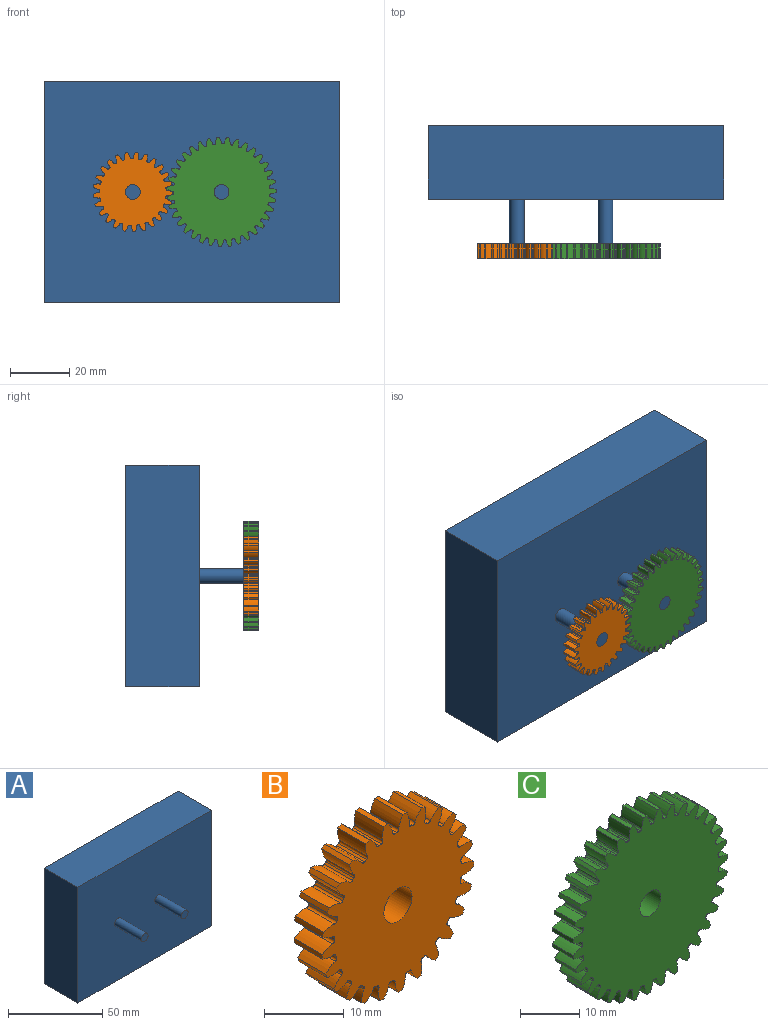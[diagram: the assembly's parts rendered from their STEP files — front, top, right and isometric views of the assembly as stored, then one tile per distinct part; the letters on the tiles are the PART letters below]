
ASSEMBLY  parts=3 mates=2
PART A: 10 faces, bbox 100x45x75 mm
  f0: plane 75x25mm, normal (1,0,0), area 1875mm2, adj f1,f3,f4,f5
  f1: plane 100x25mm, normal (0,0,1), area 2500mm2, adj f0,f2,f4,f5
  f2: plane 75x25mm, normal (-1,0,0), area 1875mm2, adj f1,f3,f4,f5
  f3: plane 100x25mm, normal (0,0,-1), area 2500mm2, adj f0,f2,f4,f5
  f4: plane 100x75mm, normal (0,1,0), area 7500mm2, adj f0,f1,f2,f3
  f5: plane 100x75mm, normal (0,-1,0), area 7460.7mm2, adj f0,f1,f2,f3,f6,f8
  f6: cylinder r=2.5mm len=20mm, axis (0,1,0), area 314.2mm2, adj f5,f7
  f7: plane 5x5mm, normal (0,-1,0), area 19.6mm2, adj f6
  f8: cylinder r=2.5mm len=20mm, axis (0,1,0), area 314.2mm2, adj f5,f9
  f9: plane 5x5mm, normal (0,-1,0), area 19.6mm2, adj f8
PART B: 153 faces, bbox 27x5x27 mm
  f0: extruded ~5x1.91mm, area 10.1mm2, adj f100,f101,f102,f103
  f1: cylinder r=11.25mm len=5mm, axis (0,1,0), area 1.9mm2, adj f101,f102,f103,f104
  f2: extruded ~5x1.76mm, area 10.1mm2, adj f3,f101,f102,f104
  f3: cylinder r=13.5mm len=5mm, axis (0,1,0), area 3.6mm2, adj f2,f4,f101,f102
  f4: extruded ~5x2mm, area 10.1mm2, adj f3,f101,f102,f105
  f5: cylinder r=11.25mm len=5mm, axis (0,1,0), area 1.9mm2, adj f101,f102,f105,f106
  f6: extruded ~5x1.47mm, area 10.1mm2, adj f7,f101,f102,f106
  f7: cylinder r=13.5mm len=5mm, axis (0,1,0), area 3.6mm2, adj f6,f8,f101,f102
  f8: extruded ~5x1.96mm, area 10.1mm2, adj f7,f101,f102,f107
  f9: cylinder r=11.25mm len=5mm, axis (0,1,0), area 1.9mm2, adj f101,f102,f107,f108
  f10: extruded ~5x1.68mm, area 10.1mm2, adj f11,f101,f102,f108
  f11: cylinder r=13.5mm len=5mm, axis (0,1,0), area 3.6mm2, adj f10,f12,f101,f102
  f12: extruded ~5x1.8mm, area 10.1mm2, adj f11,f101,f102,f109
  f13: cylinder r=11.25mm len=5mm, axis (0,1,0), area 1.9mm2, adj f101,f102,f109,f110
  f14: extruded ~5x1.9mm, area 10.1mm2, adj f15,f101,f102,f110
  f15: cylinder r=13.5mm len=5mm, axis (0,1,0), area 3.6mm2, adj f14,f16,f101,f102
  f16: extruded ~5x1.53mm, area 10.1mm2, adj f15,f101,f102,f111
  f17: cylinder r=11.25mm len=5mm, axis (0,1,0), area 1.9mm2, adj f101,f102,f111,f112
  f18: extruded ~5x2mm, area 10.1mm2, adj f19,f101,f102,f112
  f19: cylinder r=13.5mm len=5mm, axis (0,1,0), area 3.6mm2, adj f18,f20,f101,f102
  f20: extruded ~5x1.63mm, area 10.1mm2, adj f19,f101,f102,f113
  f21: cylinder r=11.25mm len=5mm, axis (0,1,0), area 1.9mm2, adj f101,f102,f113,f114
  f22: extruded ~5x1.97mm, area 10.1mm2, adj f23,f101,f102,f114
  f23: cylinder r=13.5mm len=5mm, axis (0,1,0), area 3.6mm2, adj f22,f24,f101,f102
  f24: extruded ~5x1.87mm, area 10.1mm2, adj f23,f101,f102,f115
  f25: cylinder r=11.25mm len=5mm, axis (0,1,0), area 1.9mm2, adj f101,f102,f115,f116
  f26: extruded ~5x1.82mm, area 10.1mm2, adj f27,f101,f102,f116
  f27: cylinder r=13.5mm len=5mm, axis (0,1,0), area 3.6mm2, adj f26,f28,f101,f102
  f28: extruded ~5x1.99mm, area 10.1mm2, adj f27,f101,f102,f117
  f29: cylinder r=11.25mm len=5mm, axis (0,1,0), area 1.9mm2, adj f101,f102,f117,f118
  f30: extruded ~5x1.55mm, area 10.1mm2, adj f31,f101,f102,f118
  f31: cylinder r=13.5mm len=5mm, axis (0,1,0), area 3.6mm2, adj f30,f32,f101,f102
  f32: extruded ~5x1.98mm, area 10.1mm2, adj f31,f101,f102,f119
  f33: cylinder r=11.25mm len=5mm, axis (0,1,0), area 1.9mm2, adj f101,f102,f119,f120
  f34: extruded ~5x1.61mm, area 10.1mm2, adj f35,f101,f102,f120
  f35: cylinder r=13.5mm len=5mm, axis (0,1,0), area 3.6mm2, adj f34,f36,f101,f102
  f36: extruded ~5x1.85mm, area 10.1mm2, adj f35,f101,f102,f121
  f37: cylinder r=11.25mm len=5mm, axis (0,1,0), area 1.9mm2, adj f101,f102,f121,f122
  f38: extruded ~5x1.86mm, area 10.1mm2, adj f39,f101,f102,f122
  f39: cylinder r=13.5mm len=5mm, axis (0,1,0), area 3.6mm2, adj f38,f40,f101,f102
  f40: extruded ~5x1.61mm, area 10.1mm2, adj f39,f101,f102,f123
  f41: cylinder r=11.25mm len=5mm, axis (0,1,0), area 1.9mm2, adj f101,f102,f123,f124
  f42: extruded ~5x1.98mm, area 10.1mm2, adj f43,f101,f102,f124
  f43: cylinder r=13.5mm len=5mm, axis (0,1,0), area 3.6mm2, adj f42,f44,f101,f102
  f44: extruded ~5x1.56mm, area 10.1mm2, adj f43,f101,f102,f125
  f45: cylinder r=11.25mm len=5mm, axis (0,1,0), area 1.9mm2, adj f101,f102,f125,f126
  f46: extruded ~5x1.99mm, area 10.1mm2, adj f47,f101,f102,f126
  f47: cylinder r=13.5mm len=5mm, axis (0,1,0), area 3.6mm2, adj f46,f48,f101,f102
  f48: extruded ~5x1.82mm, area 10.1mm2, adj f47,f101,f102,f127
  f49: cylinder r=11.25mm len=5mm, axis (0,1,0), area 1.9mm2, adj f101,f102,f127,f128
  f50: extruded ~5x1.87mm, area 10.1mm2, adj f51,f101,f102,f128
  f51: cylinder r=13.5mm len=5mm, axis (0,1,0), area 3.6mm2, adj f50,f52,f101,f102
  f52: extruded ~5x1.97mm, area 10.1mm2, adj f51,f101,f102,f129
  f53: cylinder r=11.25mm len=5mm, axis (0,1,0), area 1.9mm2, adj f101,f102,f129,f130
  f54: extruded ~5x1.63mm, area 10.1mm2, adj f55,f101,f102,f130
  f55: cylinder r=13.5mm len=5mm, axis (0,1,0), area 3.6mm2, adj f54,f56,f101,f102
  f56: extruded ~5x2mm, area 10.1mm2, adj f55,f101,f102,f131
  f57: cylinder r=11.25mm len=5mm, axis (0,1,0), area 1.9mm2, adj f101,f102,f131,f132
  f58: extruded ~5x1.53mm, area 10.1mm2, adj f59,f101,f102,f132
  f59: cylinder r=13.5mm len=5mm, axis (0,1,0), area 3.6mm2, adj f58,f60,f101,f102
  f60: extruded ~5x1.9mm, area 10.1mm2, adj f59,f101,f102,f133
  f61: cylinder r=11.25mm len=5mm, axis (0,1,0), area 1.9mm2, adj f101,f102,f133,f134
  f62: extruded ~5x1.81mm, area 10.1mm2, adj f63,f101,f102,f134
  f63: cylinder r=13.5mm len=5mm, axis (0,1,0), area 3.6mm2, adj f62,f64,f101,f102
  f64: extruded ~5x1.68mm, area 10.1mm2, adj f63,f101,f102,f135
  f65: cylinder r=11.25mm len=5mm, axis (0,1,0), area 1.9mm2, adj f101,f102,f135,f136
  f66: extruded ~5x1.96mm, area 10.1mm2, adj f67,f101,f102,f136
  f67: cylinder r=13.5mm len=5mm, axis (0,1,0), area 3.6mm2, adj f66,f68,f101,f102
  f68: extruded ~5x1.47mm, area 10.1mm2, adj f67,f101,f102,f137
  f69: cylinder r=11.25mm len=5mm, axis (0,1,0), area 1.9mm2, adj f101,f102,f137,f138
  f70: extruded ~5x2mm, area 10.1mm2, adj f71,f101,f102,f138
  f71: cylinder r=13.5mm len=5mm, axis (0,1,0), area 3.6mm2, adj f70,f72,f101,f102
  f72: extruded ~5x1.76mm, area 10.1mm2, adj f71,f101,f102,f139
  f73: cylinder r=11.25mm len=5mm, axis (0,1,0), area 1.9mm2, adj f101,f102,f139,f140
  f74: extruded ~5x1.91mm, area 10.1mm2, adj f75,f101,f102,f140
  f75: cylinder r=13.5mm len=5mm, axis (0,1,0), area 3.6mm2, adj f74,f76,f101,f102
  f76: extruded ~5x1.94mm, area 10.1mm2, adj f75,f101,f102,f141
  f77: cylinder r=11.25mm len=5mm, axis (0,1,0), area 1.9mm2, adj f101,f102,f141,f142
  f78: extruded ~5x1.7mm, area 10.1mm2, adj f79,f101,f102,f142
  f79: cylinder r=13.5mm len=5mm, axis (0,1,0), area 3.6mm2, adj f78,f80,f101,f102
  f80: extruded ~5x2mm, area 10.1mm2, adj f79,f101,f102,f143
  f81: cylinder r=11.25mm len=5mm, axis (0,1,0), area 1.9mm2, adj f101,f102,f143,f144
  f82: extruded ~5x1.45mm, area 10.1mm2, adj f83,f101,f102,f144
  f83: cylinder r=13.5mm len=5mm, axis (0,1,0), area 3.6mm2, adj f82,f84,f101,f102
  f84: extruded ~5x1.93mm, area 10.1mm2, adj f83,f101,f102,f145
  f85: cylinder r=11.25mm len=5mm, axis (0,1,0), area 1.9mm2, adj f101,f102,f145,f146
  f86: extruded ~5x1.75mm, area 10.1mm2, adj f87,f101,f102,f146
  f87: cylinder r=13.5mm len=5mm, axis (0,1,0), area 3.6mm2, adj f86,f88,f101,f102
  f88: extruded ~5x1.74mm, area 10.1mm2, adj f87,f101,f102,f147
  f89: cylinder r=11.25mm len=5mm, axis (0,1,0), area 1.9mm2, adj f101,f102,f147,f148
  f90: extruded ~5x1.94mm, area 10.1mm2, adj f91,f101,f102,f148
  f91: cylinder r=13.5mm len=5mm, axis (0,1,0), area 3.6mm2, adj f90,f92,f101,f102
  f92: extruded ~5x1.45mm, area 10.1mm2, adj f91,f101,f102,f149
  f93: cylinder r=11.25mm len=5mm, axis (0,1,0), area 1.9mm2, adj f101,f102,f149,f150
  f94: extruded ~5x2mm, area 10.1mm2, adj f95,f101,f102,f150
  f95: cylinder r=13.5mm len=5mm, axis (0,1,0), area 3.6mm2, adj f94,f96,f101,f102
  f96: extruded ~5x1.7mm, area 10.1mm2, adj f95,f101,f102,f151
  f97: cylinder r=11.25mm len=5mm, axis (0,1,0), area 1.9mm2, adj f101,f102,f151,f152
  f98: extruded ~5x1.94mm, area 10.1mm2, adj f100,f101,f102,f152
  f99: cylinder r=2.5mm len=5mm, axis (0,1,0), area 78.5mm2, adj f101,f102
  f100: cylinder r=13.5mm len=5mm, axis (0,1,0), area 3.6mm2, adj f0,f98,f101,f102
  f101: plane 26.98x26.97mm, normal (0,-1,0), area 463.9mm2, adj f0,f1,f2,f3,f4,f5,f6,f7
  f102: plane 26.98x26.97mm, normal (0,1,0), area 463.9mm2, adj f0,f1,f2,f3,f4,f5,f6,f7
  f103: cylinder r=0.36mm len=5mm, axis (0,1,0), area 2.8mm2, adj f0,f1,f101,f102
  f104: cylinder r=0.36mm len=5mm, axis (0,1,0), area 2.8mm2, adj f1,f2,f101,f102
  f105: cylinder r=0.36mm len=5mm, axis (0,1,0), area 2.8mm2, adj f4,f5,f101,f102
  f106: cylinder r=0.36mm len=5mm, axis (0,1,0), area 2.8mm2, adj f5,f6,f101,f102
  f107: cylinder r=0.36mm len=5mm, axis (0,1,0), area 2.8mm2, adj f8,f9,f101,f102
  f108: cylinder r=0.36mm len=5mm, axis (0,1,0), area 2.8mm2, adj f9,f10,f101,f102
  f109: cylinder r=0.36mm len=5mm, axis (0,1,0), area 2.8mm2, adj f12,f13,f101,f102
  f110: cylinder r=0.36mm len=5mm, axis (0,1,0), area 2.8mm2, adj f13,f14,f101,f102
  f111: cylinder r=0.36mm len=5mm, axis (0,1,0), area 2.8mm2, adj f16,f17,f101,f102
  f112: cylinder r=0.36mm len=5mm, axis (0,1,0), area 2.8mm2, adj f17,f18,f101,f102
  f113: cylinder r=0.36mm len=5mm, axis (0,1,0), area 2.8mm2, adj f20,f21,f101,f102
  f114: cylinder r=0.36mm len=5mm, axis (0,1,0), area 2.8mm2, adj f21,f22,f101,f102
  f115: cylinder r=0.36mm len=5mm, axis (0,1,0), area 2.8mm2, adj f24,f25,f101,f102
  f116: cylinder r=0.36mm len=5mm, axis (0,1,0), area 2.8mm2, adj f25,f26,f101,f102
  f117: cylinder r=0.36mm len=5mm, axis (0,1,0), area 2.8mm2, adj f28,f29,f101,f102
  f118: cylinder r=0.36mm len=5mm, axis (0,1,0), area 2.8mm2, adj f29,f30,f101,f102
  f119: cylinder r=0.36mm len=5mm, axis (0,1,0), area 2.8mm2, adj f32,f33,f101,f102
  f120: cylinder r=0.36mm len=5mm, axis (0,1,0), area 2.8mm2, adj f33,f34,f101,f102
  f121: cylinder r=0.36mm len=5mm, axis (0,1,0), area 2.8mm2, adj f36,f37,f101,f102
  f122: cylinder r=0.36mm len=5mm, axis (0,1,0), area 2.8mm2, adj f37,f38,f101,f102
  f123: cylinder r=0.36mm len=5mm, axis (0,1,0), area 2.8mm2, adj f40,f41,f101,f102
  f124: cylinder r=0.36mm len=5mm, axis (0,1,0), area 2.8mm2, adj f41,f42,f101,f102
  f125: cylinder r=0.36mm len=5mm, axis (0,1,0), area 2.8mm2, adj f44,f45,f101,f102
  f126: cylinder r=0.36mm len=5mm, axis (0,1,0), area 2.8mm2, adj f45,f46,f101,f102
  f127: cylinder r=0.36mm len=5mm, axis (0,1,0), area 2.8mm2, adj f48,f49,f101,f102
  f128: cylinder r=0.36mm len=5mm, axis (0,1,0), area 2.8mm2, adj f49,f50,f101,f102
  f129: cylinder r=0.36mm len=5mm, axis (0,1,0), area 2.8mm2, adj f52,f53,f101,f102
  f130: cylinder r=0.36mm len=5mm, axis (0,1,0), area 2.8mm2, adj f53,f54,f101,f102
  f131: cylinder r=0.36mm len=5mm, axis (0,1,0), area 2.8mm2, adj f56,f57,f101,f102
  f132: cylinder r=0.36mm len=5mm, axis (0,1,0), area 2.8mm2, adj f57,f58,f101,f102
  f133: cylinder r=0.36mm len=5mm, axis (0,1,0), area 2.8mm2, adj f60,f61,f101,f102
  f134: cylinder r=0.36mm len=5mm, axis (0,1,0), area 2.8mm2, adj f61,f62,f101,f102
  f135: cylinder r=0.36mm len=5mm, axis (0,1,0), area 2.8mm2, adj f64,f65,f101,f102
  f136: cylinder r=0.36mm len=5mm, axis (0,1,0), area 2.8mm2, adj f65,f66,f101,f102
  f137: cylinder r=0.36mm len=5mm, axis (0,1,0), area 2.8mm2, adj f68,f69,f101,f102
  f138: cylinder r=0.36mm len=5mm, axis (0,1,0), area 2.8mm2, adj f69,f70,f101,f102
  f139: cylinder r=0.36mm len=5mm, axis (0,1,0), area 2.8mm2, adj f72,f73,f101,f102
  f140: cylinder r=0.36mm len=5mm, axis (0,1,0), area 2.8mm2, adj f73,f74,f101,f102
  f141: cylinder r=0.36mm len=5mm, axis (0,1,0), area 2.8mm2, adj f76,f77,f101,f102
  f142: cylinder r=0.36mm len=5mm, axis (0,1,0), area 2.8mm2, adj f77,f78,f101,f102
  f143: cylinder r=0.36mm len=5mm, axis (0,1,0), area 2.8mm2, adj f80,f81,f101,f102
  f144: cylinder r=0.36mm len=5mm, axis (0,1,0), area 2.8mm2, adj f81,f82,f101,f102
  f145: cylinder r=0.36mm len=5mm, axis (0,1,0), area 2.8mm2, adj f84,f85,f101,f102
  f146: cylinder r=0.36mm len=5mm, axis (0,1,0), area 2.8mm2, adj f85,f86,f101,f102
  f147: cylinder r=0.36mm len=5mm, axis (0,1,0), area 2.8mm2, adj f88,f89,f101,f102
  f148: cylinder r=0.36mm len=5mm, axis (0,1,0), area 2.8mm2, adj f89,f90,f101,f102
  f149: cylinder r=0.36mm len=5mm, axis (0,1,0), area 2.8mm2, adj f92,f93,f101,f102
  f150: cylinder r=0.36mm len=5mm, axis (0,1,0), area 2.8mm2, adj f93,f94,f101,f102
  f151: cylinder r=0.36mm len=5mm, axis (0,1,0), area 2.8mm2, adj f96,f97,f101,f102
  f152: cylinder r=0.36mm len=5mm, axis (0,1,0), area 2.8mm2, adj f97,f98,f101,f102
PART C: 213 faces, bbox 37x5x37 mm
  f0: extruded ~5x2mm, area 10.5mm2, adj f140,f141,f142,f143
  f1: cylinder r=16.25mm len=5mm, axis (0,1,0), area 1.8mm2, adj f141,f142,f143,f144
  f2: extruded ~5x1.83mm, area 10.5mm2, adj f3,f141,f142,f144
  f3: cylinder r=18.5mm len=5mm, axis (0,1,0), area 3.7mm2, adj f2,f4,f141,f142
  f4: extruded ~5x2.07mm, area 10.5mm2, adj f3,f141,f142,f145
  f5: cylinder r=16.25mm len=5mm, axis (0,1,0), area 1.8mm2, adj f141,f142,f145,f146
  f6: extruded ~5x1.63mm, area 10.5mm2, adj f7,f141,f142,f146
  f7: cylinder r=18.5mm len=5mm, axis (0,1,0), area 3.7mm2, adj f6,f8,f141,f142
  f8: extruded ~5x2.07mm, area 10.5mm2, adj f7,f141,f142,f147
  f9: cylinder r=16.25mm len=5mm, axis (0,1,0), area 1.8mm2, adj f141,f142,f147,f148
  f10: extruded ~5x1.57mm, area 10.5mm2, adj f11,f141,f142,f148
  f11: cylinder r=18.5mm len=5mm, axis (0,1,0), area 3.7mm2, adj f10,f12,f141,f142
  f12: extruded ~5x2.01mm, area 10.5mm2, adj f11,f141,f142,f149
  f13: cylinder r=16.25mm len=5mm, axis (0,1,0), area 1.8mm2, adj f141,f142,f149,f150
  f14: extruded ~5x1.79mm, area 10.5mm2, adj f15,f141,f142,f150
  f15: cylinder r=18.5mm len=5mm, axis (0,1,0), area 3.7mm2, adj f14,f16,f141,f142
  f16: extruded ~5x1.88mm, area 10.5mm2, adj f15,f141,f142,f151
  f17: cylinder r=16.25mm len=5mm, axis (0,1,0), area 1.8mm2, adj f141,f142,f151,f152
  f18: extruded ~5x1.95mm, area 10.5mm2, adj f19,f141,f142,f152
  f19: cylinder r=18.5mm len=5mm, axis (0,1,0), area 3.7mm2, adj f18,f20,f141,f142
  f20: extruded ~5x1.69mm, area 10.5mm2, adj f19,f141,f142,f153
  f21: cylinder r=16.25mm len=5mm, axis (0,1,0), area 1.8mm2, adj f141,f142,f153,f154
  f22: extruded ~5x2.05mm, area 10.5mm2, adj f23,f141,f142,f154
  f23: cylinder r=18.5mm len=5mm, axis (0,1,0), area 3.7mm2, adj f22,f24,f141,f142
  f24: extruded ~5x1.49mm, area 10.5mm2, adj f23,f141,f142,f155
  f25: cylinder r=16.25mm len=5mm, axis (0,1,0), area 1.8mm2, adj f141,f142,f155,f156
  f26: extruded ~5x2.08mm, area 10.5mm2, adj f27,f141,f142,f156
  f27: cylinder r=18.5mm len=5mm, axis (0,1,0), area 3.7mm2, adj f26,f28,f141,f142
  f28: extruded ~5x1.73mm, area 10.5mm2, adj f27,f141,f142,f157
  f29: cylinder r=16.25mm len=5mm, axis (0,1,0), area 1.8mm2, adj f141,f142,f157,f158
  f30: extruded ~5x2.05mm, area 10.5mm2, adj f31,f141,f142,f158
  f31: cylinder r=18.5mm len=5mm, axis (0,1,0), area 3.7mm2, adj f30,f32,f141,f142
  f32: extruded ~5x1.91mm, area 10.5mm2, adj f31,f141,f142,f159
  f33: cylinder r=16.25mm len=5mm, axis (0,1,0), area 1.8mm2, adj f141,f142,f159,f160
  f34: extruded ~5x1.95mm, area 10.5mm2, adj f35,f141,f142,f160
  f35: cylinder r=18.5mm len=5mm, axis (0,1,0), area 3.7mm2, adj f34,f36,f141,f142
  f36: extruded ~5x2.03mm, area 10.5mm2, adj f35,f141,f142,f161
  f37: cylinder r=16.25mm len=5mm, axis (0,1,0), area 1.8mm2, adj f141,f142,f161,f162
  f38: extruded ~5x1.79mm, area 10.5mm2, adj f39,f141,f142,f162
  f39: cylinder r=18.5mm len=5mm, axis (0,1,0), area 3.7mm2, adj f38,f40,f141,f142
  f40: extruded ~5x2.08mm, area 10.5mm2, adj f39,f141,f142,f163
  f41: cylinder r=16.25mm len=5mm, axis (0,1,0), area 1.8mm2, adj f141,f142,f163,f164
  f42: extruded ~5x1.57mm, area 10.5mm2, adj f43,f141,f142,f164
  f43: cylinder r=18.5mm len=5mm, axis (0,1,0), area 3.7mm2, adj f42,f44,f141,f142
  f44: extruded ~5x2.06mm, area 10.5mm2, adj f43,f141,f142,f165
  f45: cylinder r=16.25mm len=5mm, axis (0,1,0), area 1.8mm2, adj f141,f142,f165,f166
  f46: extruded ~5x1.63mm, area 10.5mm2, adj f47,f141,f142,f166
  f47: cylinder r=18.5mm len=5mm, axis (0,1,0), area 3.7mm2, adj f46,f48,f141,f142
  f48: extruded ~5x1.98mm, area 10.5mm2, adj f47,f141,f142,f167
  f49: cylinder r=16.25mm len=5mm, axis (0,1,0), area 1.8mm2, adj f141,f142,f167,f168
  f50: extruded ~5x1.83mm, area 10.5mm2, adj f51,f141,f142,f168
  f51: cylinder r=18.5mm len=5mm, axis (0,1,0), area 3.7mm2, adj f50,f52,f141,f142
  f52: extruded ~5x1.84mm, area 10.5mm2, adj f51,f141,f142,f169
  f53: cylinder r=16.25mm len=5mm, axis (0,1,0), area 1.8mm2, adj f141,f142,f169,f170
  f54: extruded ~5x1.98mm, area 10.5mm2, adj f55,f141,f142,f170
  f55: cylinder r=18.5mm len=5mm, axis (0,1,0), area 3.7mm2, adj f54,f56,f141,f142
  f56: extruded ~5x1.64mm, area 10.5mm2, adj f55,f141,f142,f171
  f57: cylinder r=16.25mm len=5mm, axis (0,1,0), area 1.8mm2, adj f141,f142,f171,f172
  f58: extruded ~5x2.06mm, area 10.5mm2, adj f59,f141,f142,f172
  f59: cylinder r=18.5mm len=5mm, axis (0,1,0), area 3.7mm2, adj f58,f60,f141,f142
  f60: extruded ~5x1.56mm, area 10.5mm2, adj f59,f141,f142,f173
  f61: cylinder r=16.25mm len=5mm, axis (0,1,0), area 1.8mm2, adj f141,f142,f173,f174
  f62: extruded ~5x2.08mm, area 10.5mm2, adj f63,f141,f142,f174
  f63: cylinder r=18.5mm len=5mm, axis (0,1,0), area 3.7mm2, adj f62,f64,f141,f142
  f64: extruded ~5x1.78mm, area 10.5mm2, adj f63,f141,f142,f175
  f65: cylinder r=16.25mm len=5mm, axis (0,1,0), area 1.8mm2, adj f141,f142,f175,f176
  f66: extruded ~5x2.03mm, area 10.5mm2, adj f67,f141,f142,f176
  f67: cylinder r=18.5mm len=5mm, axis (0,1,0), area 3.7mm2, adj f66,f68,f141,f142
  f68: extruded ~5x1.94mm, area 10.5mm2, adj f67,f141,f142,f177
  f69: cylinder r=16.25mm len=5mm, axis (0,1,0), area 1.8mm2, adj f141,f142,f177,f178
  f70: extruded ~5x1.91mm, area 10.5mm2, adj f71,f141,f142,f178
  f71: cylinder r=18.5mm len=5mm, axis (0,1,0), area 3.7mm2, adj f70,f72,f141,f142
  f72: extruded ~5x2.04mm, area 10.5mm2, adj f71,f141,f142,f179
  f73: cylinder r=16.25mm len=5mm, axis (0,1,0), area 1.8mm2, adj f141,f142,f179,f180
  f74: extruded ~5x1.74mm, area 10.5mm2, adj f75,f141,f142,f180
  f75: cylinder r=18.5mm len=5mm, axis (0,1,0), area 3.7mm2, adj f74,f76,f141,f142
  f76: extruded ~5x2.08mm, area 10.5mm2, adj f75,f141,f142,f181
  f77: cylinder r=16.25mm len=5mm, axis (0,1,0), area 1.8mm2, adj f141,f142,f181,f182
  f78: extruded ~5x1.5mm, area 10.5mm2, adj f79,f141,f142,f182
  f79: cylinder r=18.5mm len=5mm, axis (0,1,0), area 3.7mm2, adj f78,f80,f141,f142
  f80: extruded ~5x2.05mm, area 10.5mm2, adj f79,f141,f142,f183
  f81: cylinder r=16.25mm len=5mm, axis (0,1,0), area 1.8mm2, adj f141,f142,f183,f184
  f82: extruded ~5x1.69mm, area 10.5mm2, adj f83,f141,f142,f184
  f83: cylinder r=18.5mm len=5mm, axis (0,1,0), area 3.7mm2, adj f82,f84,f141,f142
  f84: extruded ~5x1.95mm, area 10.5mm2, adj f83,f141,f142,f185
  f85: cylinder r=16.25mm len=5mm, axis (0,1,0), area 1.8mm2, adj f141,f142,f185,f186
  f86: extruded ~5x1.88mm, area 10.5mm2, adj f87,f141,f142,f186
  f87: cylinder r=18.5mm len=5mm, axis (0,1,0), area 3.7mm2, adj f86,f88,f141,f142
  f88: extruded ~5x1.79mm, area 10.5mm2, adj f87,f141,f142,f187
  f89: cylinder r=16.25mm len=5mm, axis (0,1,0), area 1.8mm2, adj f141,f142,f187,f188
  f90: extruded ~5x2.01mm, area 10.5mm2, adj f91,f141,f142,f188
  f91: cylinder r=18.5mm len=5mm, axis (0,1,0), area 3.7mm2, adj f90,f92,f141,f142
  f92: extruded ~5x1.58mm, area 10.5mm2, adj f91,f141,f142,f189
  f93: cylinder r=16.25mm len=5mm, axis (0,1,0), area 1.8mm2, adj f141,f142,f189,f190
  f94: extruded ~5x2.07mm, area 10.5mm2, adj f95,f141,f142,f190
  f95: cylinder r=18.5mm len=5mm, axis (0,1,0), area 3.7mm2, adj f94,f96,f141,f142
  f96: extruded ~5x1.62mm, area 10.5mm2, adj f95,f141,f142,f191
  f97: cylinder r=16.25mm len=5mm, axis (0,1,0), area 1.8mm2, adj f141,f142,f191,f192
  f98: extruded ~5x2.07mm, area 10.5mm2, adj f99,f141,f142,f192
  f99: cylinder r=18.5mm len=5mm, axis (0,1,0), area 3.7mm2, adj f98,f100,f141,f142
  f100: extruded ~5x1.83mm, area 10.5mm2, adj f99,f141,f142,f193
  f101: cylinder r=16.25mm len=5mm, axis (0,1,0), area 1.8mm2, adj f141,f142,f193,f194
  f102: extruded ~5x2.01mm, area 10.5mm2, adj f103,f141,f142,f194
  f103: cylinder r=18.5mm len=5mm, axis (0,1,0), area 3.7mm2, adj f102,f104,f141,f142
  f104: extruded ~5x1.97mm, area 10.5mm2, adj f103,f141,f142,f195
  f105: cylinder r=16.25mm len=5mm, axis (0,1,0), area 1.8mm2, adj f141,f142,f195,f196
  f106: extruded ~5x1.87mm, area 10.5mm2, adj f107,f141,f142,f196
  f107: cylinder r=18.5mm len=5mm, axis (0,1,0), area 3.7mm2, adj f106,f108,f141,f142
  f108: extruded ~5x2.06mm, area 10.5mm2, adj f107,f141,f142,f197
  f109: cylinder r=16.25mm len=5mm, axis (0,1,0), area 1.8mm2, adj f141,f142,f197,f198
  f110: extruded ~5x1.68mm, area 10.5mm2, adj f111,f141,f142,f198
  f111: cylinder r=18.5mm len=5mm, axis (0,1,0), area 3.7mm2, adj f110,f112,f141,f142
  f112: extruded ~5x2.08mm, area 10.5mm2, adj f111,f141,f142,f199
  f113: cylinder r=16.25mm len=5mm, axis (0,1,0), area 1.8mm2, adj f141,f142,f199,f200
  f114: extruded ~5x1.51mm, area 10.5mm2, adj f115,f141,f142,f200
  f115: cylinder r=18.5mm len=5mm, axis (0,1,0), area 3.7mm2, adj f114,f116,f141,f142
  f116: extruded ~5x2.03mm, area 10.5mm2, adj f115,f141,f142,f201
  f117: cylinder r=16.25mm len=5mm, axis (0,1,0), area 1.8mm2, adj f141,f142,f201,f202
  f118: extruded ~5x1.74mm, area 10.5mm2, adj f119,f141,f142,f202
  f119: cylinder r=18.5mm len=5mm, axis (0,1,0), area 3.7mm2, adj f118,f120,f141,f142
  f120: extruded ~5x1.92mm, area 10.5mm2, adj f119,f141,f142,f203
  f121: cylinder r=16.25mm len=5mm, axis (0,1,0), area 1.8mm2, adj f141,f142,f203,f204
  f122: extruded ~5x1.91mm, area 10.5mm2, adj f123,f141,f142,f204
  f123: cylinder r=18.5mm len=5mm, axis (0,1,0), area 3.7mm2, adj f122,f124,f141,f142
  f124: extruded ~5x1.75mm, area 10.5mm2, adj f123,f141,f142,f205
  f125: cylinder r=16.25mm len=5mm, axis (0,1,0), area 1.8mm2, adj f141,f142,f205,f206
  f126: extruded ~5x2.03mm, area 10.5mm2, adj f127,f141,f142,f206
  f127: cylinder r=18.5mm len=5mm, axis (0,1,0), area 3.7mm2, adj f126,f128,f141,f142
  f128: extruded ~5x1.51mm, area 10.5mm2, adj f127,f141,f142,f207
  f129: cylinder r=16.25mm len=5mm, axis (0,1,0), area 1.8mm2, adj f141,f142,f207,f208
  f130: extruded ~5x2.08mm, area 10.5mm2, adj f131,f141,f142,f208
  f131: cylinder r=18.5mm len=5mm, axis (0,1,0), area 3.7mm2, adj f130,f132,f141,f142
  f132: extruded ~5x1.67mm, area 10.5mm2, adj f131,f141,f142,f209
  f133: cylinder r=16.25mm len=5mm, axis (0,1,0), area 1.8mm2, adj f141,f142,f209,f210
  f134: extruded ~5x2.06mm, area 10.5mm2, adj f135,f141,f142,f210
  f135: cylinder r=18.5mm len=5mm, axis (0,1,0), area 3.7mm2, adj f134,f136,f141,f142
  f136: extruded ~5x1.87mm, area 10.5mm2, adj f135,f141,f142,f211
  f137: cylinder r=16.25mm len=5mm, axis (0,1,0), area 1.8mm2, adj f141,f142,f211,f212
  f138: extruded ~5x1.98mm, area 10.5mm2, adj f140,f141,f142,f212
  f139: cylinder r=2.5mm len=5mm, axis (0,1,0), area 78.5mm2, adj f141,f142
  f140: cylinder r=18.5mm len=5mm, axis (0,1,0), area 3.7mm2, adj f0,f138,f141,f142
  f141: plane 36.98x36.98mm, normal (0,-1,0), area 933.6mm2, adj f0,f1,f2,f3,f4,f5,f6,f7
  f142: plane 36.98x36.98mm, normal (0,1,0), area 933.6mm2, adj f0,f1,f2,f3,f4,f5,f6,f7
  f143: cylinder r=0.32mm len=5mm, axis (0,1,0), area 2.3mm2, adj f0,f1,f141,f142
  f144: cylinder r=0.32mm len=5mm, axis (0,1,0), area 2.3mm2, adj f1,f2,f141,f142
  f145: cylinder r=0.32mm len=5mm, axis (0,1,0), area 2.3mm2, adj f4,f5,f141,f142
  f146: cylinder r=0.32mm len=5mm, axis (0,1,0), area 2.3mm2, adj f5,f6,f141,f142
  f147: cylinder r=0.32mm len=5mm, axis (0,1,0), area 2.3mm2, adj f8,f9,f141,f142
  f148: cylinder r=0.32mm len=5mm, axis (0,1,0), area 2.3mm2, adj f9,f10,f141,f142
  f149: cylinder r=0.32mm len=5mm, axis (0,1,0), area 2.3mm2, adj f12,f13,f141,f142
  f150: cylinder r=0.32mm len=5mm, axis (0,1,0), area 2.3mm2, adj f13,f14,f141,f142
  f151: cylinder r=0.32mm len=5mm, axis (0,1,0), area 2.3mm2, adj f16,f17,f141,f142
  f152: cylinder r=0.32mm len=5mm, axis (0,1,0), area 2.3mm2, adj f17,f18,f141,f142
  f153: cylinder r=0.32mm len=5mm, axis (0,1,0), area 2.3mm2, adj f20,f21,f141,f142
  f154: cylinder r=0.32mm len=5mm, axis (0,1,0), area 2.3mm2, adj f21,f22,f141,f142
  f155: cylinder r=0.32mm len=5mm, axis (0,1,0), area 2.3mm2, adj f24,f25,f141,f142
  f156: cylinder r=0.32mm len=5mm, axis (0,1,0), area 2.3mm2, adj f25,f26,f141,f142
  f157: cylinder r=0.32mm len=5mm, axis (0,1,0), area 2.3mm2, adj f28,f29,f141,f142
  f158: cylinder r=0.32mm len=5mm, axis (0,1,0), area 2.3mm2, adj f29,f30,f141,f142
  f159: cylinder r=0.32mm len=5mm, axis (0,1,0), area 2.3mm2, adj f32,f33,f141,f142
  f160: cylinder r=0.32mm len=5mm, axis (0,1,0), area 2.3mm2, adj f33,f34,f141,f142
  f161: cylinder r=0.32mm len=5mm, axis (0,1,0), area 2.3mm2, adj f36,f37,f141,f142
  f162: cylinder r=0.32mm len=5mm, axis (0,1,0), area 2.3mm2, adj f37,f38,f141,f142
  f163: cylinder r=0.32mm len=5mm, axis (0,1,0), area 2.3mm2, adj f40,f41,f141,f142
  f164: cylinder r=0.32mm len=5mm, axis (0,1,0), area 2.3mm2, adj f41,f42,f141,f142
  f165: cylinder r=0.32mm len=5mm, axis (0,1,0), area 2.3mm2, adj f44,f45,f141,f142
  f166: cylinder r=0.32mm len=5mm, axis (0,1,0), area 2.3mm2, adj f45,f46,f141,f142
  f167: cylinder r=0.32mm len=5mm, axis (0,1,0), area 2.3mm2, adj f48,f49,f141,f142
  f168: cylinder r=0.32mm len=5mm, axis (0,1,0), area 2.3mm2, adj f49,f50,f141,f142
  f169: cylinder r=0.32mm len=5mm, axis (0,1,0), area 2.3mm2, adj f52,f53,f141,f142
  f170: cylinder r=0.32mm len=5mm, axis (0,1,0), area 2.3mm2, adj f53,f54,f141,f142
  f171: cylinder r=0.32mm len=5mm, axis (0,1,0), area 2.3mm2, adj f56,f57,f141,f142
  f172: cylinder r=0.32mm len=5mm, axis (0,1,0), area 2.3mm2, adj f57,f58,f141,f142
  f173: cylinder r=0.32mm len=5mm, axis (0,1,0), area 2.3mm2, adj f60,f61,f141,f142
  f174: cylinder r=0.32mm len=5mm, axis (0,1,0), area 2.3mm2, adj f61,f62,f141,f142
  f175: cylinder r=0.32mm len=5mm, axis (0,1,0), area 2.3mm2, adj f64,f65,f141,f142
  f176: cylinder r=0.32mm len=5mm, axis (0,1,0), area 2.3mm2, adj f65,f66,f141,f142
  f177: cylinder r=0.32mm len=5mm, axis (0,1,0), area 2.3mm2, adj f68,f69,f141,f142
  f178: cylinder r=0.32mm len=5mm, axis (0,1,0), area 2.3mm2, adj f69,f70,f141,f142
  f179: cylinder r=0.32mm len=5mm, axis (0,1,0), area 2.3mm2, adj f72,f73,f141,f142
  f180: cylinder r=0.32mm len=5mm, axis (0,1,0), area 2.3mm2, adj f73,f74,f141,f142
  f181: cylinder r=0.32mm len=5mm, axis (0,1,0), area 2.3mm2, adj f76,f77,f141,f142
  f182: cylinder r=0.32mm len=5mm, axis (0,1,0), area 2.3mm2, adj f77,f78,f141,f142
  f183: cylinder r=0.32mm len=5mm, axis (0,1,0), area 2.3mm2, adj f80,f81,f141,f142
  f184: cylinder r=0.32mm len=5mm, axis (0,1,0), area 2.3mm2, adj f81,f82,f141,f142
  f185: cylinder r=0.32mm len=5mm, axis (0,1,0), area 2.3mm2, adj f84,f85,f141,f142
  f186: cylinder r=0.32mm len=5mm, axis (0,1,0), area 2.3mm2, adj f85,f86,f141,f142
  f187: cylinder r=0.32mm len=5mm, axis (0,1,0), area 2.3mm2, adj f88,f89,f141,f142
  f188: cylinder r=0.32mm len=5mm, axis (0,1,0), area 2.3mm2, adj f89,f90,f141,f142
  f189: cylinder r=0.32mm len=5mm, axis (0,1,0), area 2.3mm2, adj f92,f93,f141,f142
  f190: cylinder r=0.32mm len=5mm, axis (0,1,0), area 2.3mm2, adj f93,f94,f141,f142
  f191: cylinder r=0.32mm len=5mm, axis (0,1,0), area 2.3mm2, adj f96,f97,f141,f142
  f192: cylinder r=0.32mm len=5mm, axis (0,1,0), area 2.3mm2, adj f97,f98,f141,f142
  f193: cylinder r=0.32mm len=5mm, axis (0,1,0), area 2.3mm2, adj f100,f101,f141,f142
  f194: cylinder r=0.32mm len=5mm, axis (0,1,0), area 2.3mm2, adj f101,f102,f141,f142
  f195: cylinder r=0.32mm len=5mm, axis (0,1,0), area 2.3mm2, adj f104,f105,f141,f142
  f196: cylinder r=0.32mm len=5mm, axis (0,1,0), area 2.3mm2, adj f105,f106,f141,f142
  f197: cylinder r=0.32mm len=5mm, axis (0,1,0), area 2.3mm2, adj f108,f109,f141,f142
  f198: cylinder r=0.32mm len=5mm, axis (0,1,0), area 2.3mm2, adj f109,f110,f141,f142
  f199: cylinder r=0.32mm len=5mm, axis (0,1,0), area 2.3mm2, adj f112,f113,f141,f142
  f200: cylinder r=0.32mm len=5mm, axis (0,1,0), area 2.3mm2, adj f113,f114,f141,f142
  f201: cylinder r=0.32mm len=5mm, axis (0,1,0), area 2.3mm2, adj f116,f117,f141,f142
  f202: cylinder r=0.32mm len=5mm, axis (0,1,0), area 2.3mm2, adj f117,f118,f141,f142
  f203: cylinder r=0.32mm len=5mm, axis (0,1,0), area 2.3mm2, adj f120,f121,f141,f142
  f204: cylinder r=0.32mm len=5mm, axis (0,1,0), area 2.3mm2, adj f121,f122,f141,f142
  f205: cylinder r=0.32mm len=5mm, axis (0,1,0), area 2.3mm2, adj f124,f125,f141,f142
  f206: cylinder r=0.32mm len=5mm, axis (0,1,0), area 2.3mm2, adj f125,f126,f141,f142
  f207: cylinder r=0.32mm len=5mm, axis (0,1,0), area 2.3mm2, adj f128,f129,f141,f142
  f208: cylinder r=0.32mm len=5mm, axis (0,1,0), area 2.3mm2, adj f129,f130,f141,f142
  f209: cylinder r=0.32mm len=5mm, axis (0,1,0), area 2.3mm2, adj f132,f133,f141,f142
  f210: cylinder r=0.32mm len=5mm, axis (0,1,0), area 2.3mm2, adj f133,f134,f141,f142
  f211: cylinder r=0.32mm len=5mm, axis (0,1,0), area 2.3mm2, adj f136,f137,f141,f142
  f212: cylinder r=0.32mm len=5mm, axis (0,1,0), area 2.3mm2, adj f137,f138,f141,f142
PLACE A t=(-25.68,-7.5,21.73)mm fixed
PLACE B t=(-45.68,-22.5,21.73)mm
PLACE C t=(-15.68,-22.5,21.73)mm
MATE revolute C.f3 <-> A.f6  axis (0,-1,0) through (-15.68,-27.5,21.73)mm
MATE revolute B.f3 <-> A.f8  axis (0,-1,0) through (-45.68,-27.5,21.73)mm
